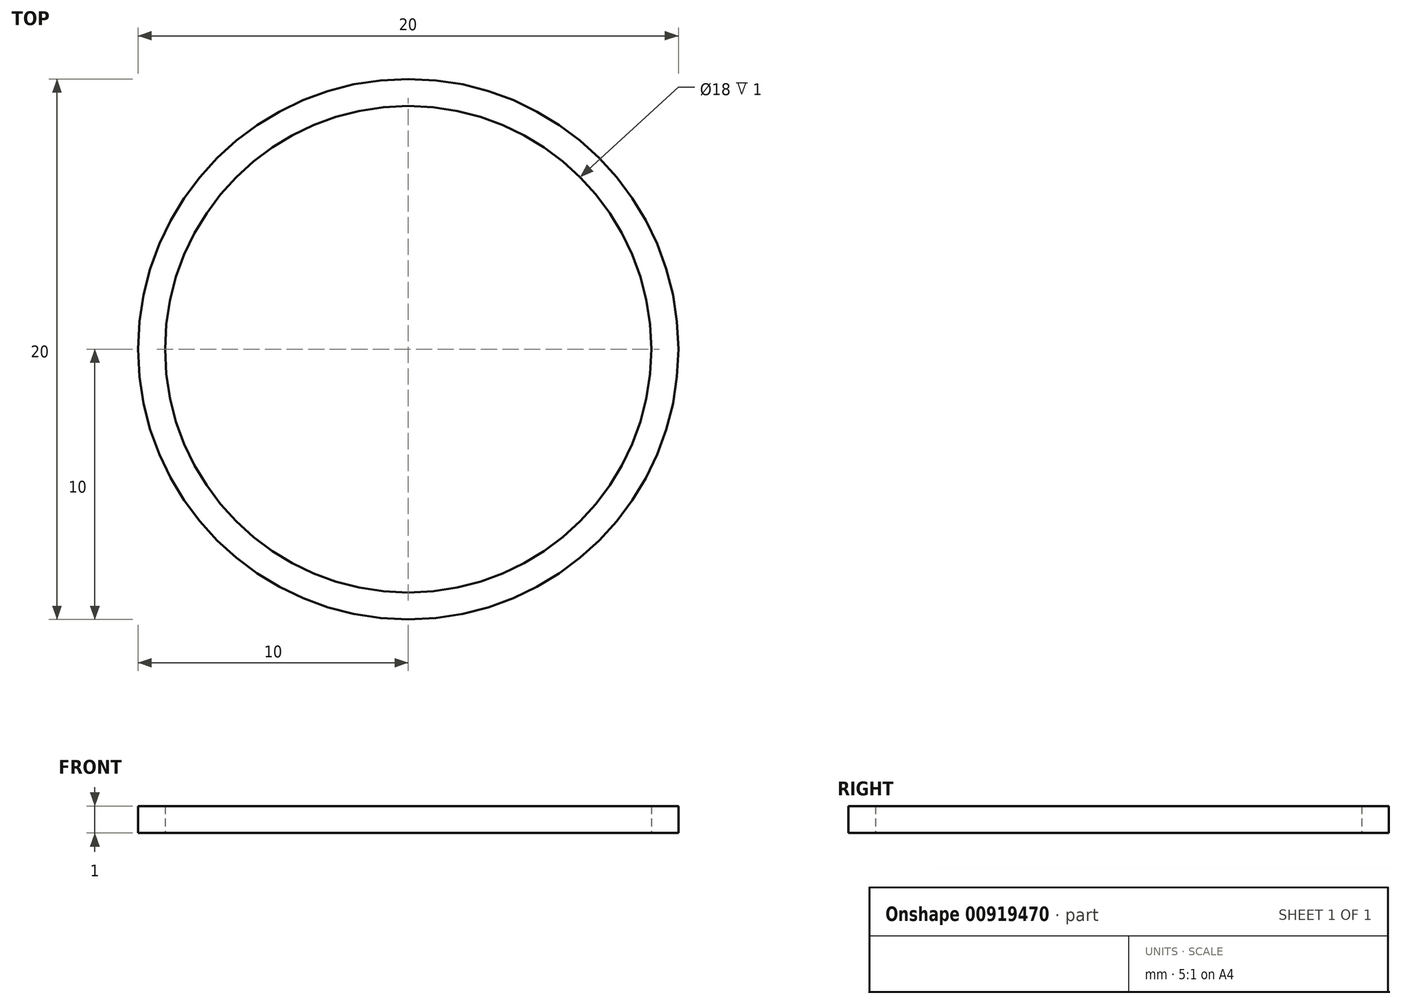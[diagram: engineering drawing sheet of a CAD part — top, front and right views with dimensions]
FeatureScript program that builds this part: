
annotation { "Feature Type Name" : "Feature", "Feature Type Description" : "" }
export const myFeature = defineFeature(function(context is Context, id is Id, definition is map)
    precondition{}
    {
        {
            var Q0;
            Q0=qCreatedBy(makeId("Top.planeOp"),FACE);
            var sketch = newSketch(context, id + "F0", { "sketchPlane" : qUnion([Q0])});
            skCircle(sketch, "E0", {"center": v(0, 0) * mm, "radius": 10 * mm});
            skCircle(sketch, "E1.0", {"center": v(0, 0) * mm, "radius": 9 * mm});
            skSolve(sketch);
        }
        {
            var Q0;
            Q0 = qSketchRegion(id + "F0", true);
            extrude(context, id + "F1", {"entities" : qUnion([Q0]), "depth" : 1 * mm, "offsetDistance" : 25 * mm});
        }
    });
